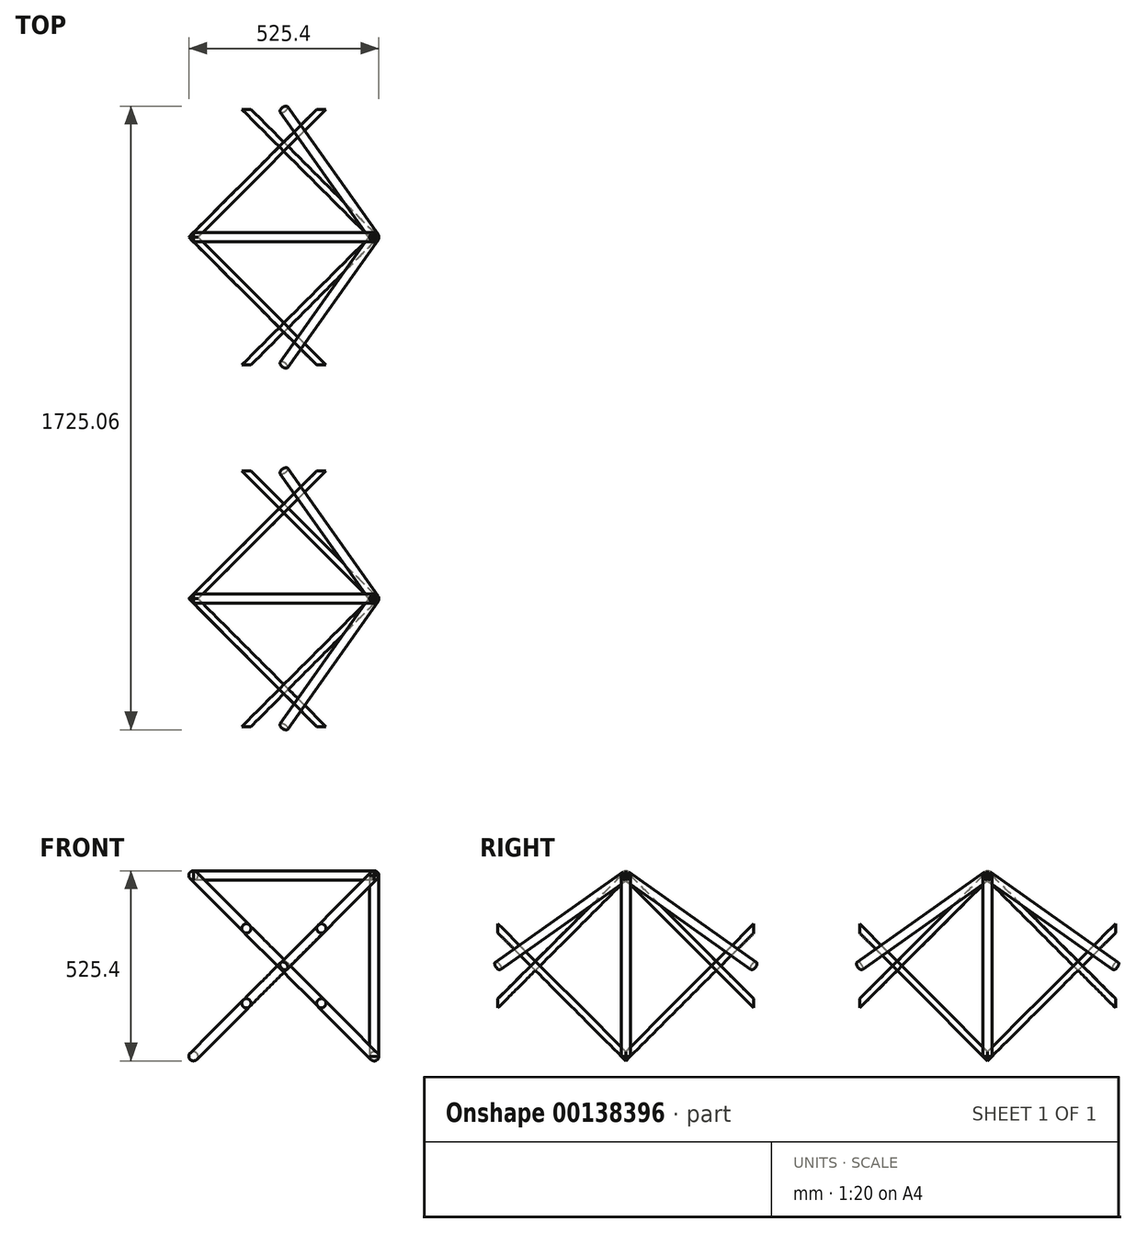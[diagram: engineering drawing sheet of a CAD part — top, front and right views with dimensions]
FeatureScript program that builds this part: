
annotation { "Feature Type Name" : "Feature", "Feature Type Description" : "" }
export const myFeature = defineFeature(function(context is Context, id is Id, definition is map)
    precondition{}
    {
        {
            var Q0;
            Q0=qCreatedBy(makeId("Front.planeOp"),FACE);
            var sketch = newSketch(context, id + "F0", { "sketchPlane" : qUnion([Q0])});
            skLineSegment(sketch, "E0.bottom", {"start": v(-250, 250) * mm, "end": v(250, 250) * mm});
            skLineSegment(sketch, "E0.top", {"start": v(-250, -250) * mm, "end": v(250, -250) * mm});
            skLineSegment(sketch, "E0.left", {"start": v(-250, 250) * mm, "end": v(-250, -250) * mm});
            skLineSegment(sketch, "E0.right", {"start": v(250, 250) * mm, "end": v(250, -250) * mm});
            skPoint(sketch, "E0.middle", {"position": v(0, 0) * mm});
            skSolve(sketch);
        }
        {
            var Q0;
            Q0=qCreatedBy(makeId("Right.planeOp"),FACE);
            var sketch = newSketch(context, id + "F1", { "sketchPlane" : qUnion([Q0])});
            skLineSegment(sketch, "E1", {"start": v(0, 0) * mm, "end": v(-500, 0) * mm});
            skSolve(sketch);
        }
        {
            var Q0;
            Q0=sQuery(id+"F0.wireOp",VERTEX,"E0.middle");
            var Q1;
            Q1=sQuery(id+"F1.wireOp",VERTEX,"E1.end");
            var Q2;
            Q2=sQuery(id+"F0.wireOp",VERTEX,"E0.right.start");
            cPlane(context, id + "F2", {"entities" : qUnion([Q0, Q1, Q2]), "cplaneType" : CPlaneType.THREE_POINT, "offset" : 25 * mm, "width" : 150 * mm, "height" : 150 * mm});
        }
        {
            var Q0;
            Q0=qCreatedBy(id+"F2.planeOp",FACE);
            var sketch = newSketch(context, id + "F3", { "sketchPlane" : qUnion([Q0])});
            skLineSegment(sketch, "E2.0", {"start": v(0, 0) * mm, "end": v(0, 500) * mm});
            skPoint(sketch, "E3.0", {"position": v(353.55, 0) * mm});
            skLineSegment(sketch, "E4", {"start": v(0, 500) * mm, "end": v(353.55, 0) * mm});
            skSolve(sketch);
        }
        {
            var Q0;
            Q0=makeQuery(id+"F0.imprint","IMPRINT",FACE,{"disambiguationData":[TD([[makeQuery(id+"F0.imprint","IMPRINT",EDGE,{"derivedFrom":sQuery(id+"F0.wireOp",EDGE,"E0.bottom")}),-1.0]])]});
            var sketch = newSketch(context, id + "F4", { "sketchPlane" : qUnion([Q0])});
            skPoint(sketch, "E5.0", {"position": v(250, 250) * mm});
            skCircle(sketch, "E6", {"center": v(250, 250) * mm, "radius": 12.7 * mm});
            skSolve(sketch);
        }
        {
            var Q0;
            Q0 = qSketchRegion(id + "F4", true);
            var Q1;
            Q1=sQuery(id+"F3.wireOp",EDGE,"E4");
            sweep(context, id + "F5", {"profiles" : qUnion([Q0]), "path" : qUnion([Q1])});
        }
        {
            var Q0;
            Q0=makeQuery(id+"F5.opSweep","SWEPT_BODY",BODY,{"disambiguationData":[OSD([sQuery(id+"F3.wireOp",EDGE,"E4"),sQuery(id+"F4.wireOp",EDGE,"E6")])]});
            var Q1;
            Q1=sQuery(id+"F1.wireOp",EDGE,"E1");
            circularPattern(context, id + "F6", {"entities" : qUnion([Q0]), "axis" : qUnion([Q1]), "angle" : 90 * degree, "instanceCount" : 4});
        }
        {
            var Q0;
            Q0=makeQuery(id+"F6.opPattern","COPY",BODY,{"derivedFrom":makeQuery(id+"F5.opSweep","SWEPT_BODY",BODY,{"disambiguationData":[OSD([sQuery(id+"F3.wireOp",EDGE,"E4"),sQuery(id+"F4.wireOp",EDGE,"E6")])]}),"instanceName":"1"});
            var Q1;
            Q1=makeQuery(id+"F6.opPattern","COPY",BODY,{"derivedFrom":makeQuery(id+"F5.opSweep","SWEPT_BODY",BODY,{"disambiguationData":[OSD([sQuery(id+"F3.wireOp",EDGE,"E4"),sQuery(id+"F4.wireOp",EDGE,"E6")])]}),"instanceName":"3"});
            var Q2;
            Q2=makeQuery(id+"F5.opSweep","SWEPT_BODY",BODY,{"disambiguationData":[OSD([sQuery(id+"F3.wireOp",EDGE,"E4"),sQuery(id+"F4.wireOp",EDGE,"E6")])]});
            var Q3;
            Q3=makeQuery(id+"F6.opPattern","COPY",BODY,{"derivedFrom":makeQuery(id+"F5.opSweep","SWEPT_BODY",BODY,{"disambiguationData":[OSD([sQuery(id+"F3.wireOp",EDGE,"E4"),sQuery(id+"F4.wireOp",EDGE,"E6")])]}),"instanceName":"2"});
            var Q4;
            Q4=makeQuery(id+"F0.imprint","IMPRINT",FACE,{"disambiguationData":[TD([[makeQuery(id+"F0.imprint","IMPRINT",EDGE,{"derivedFrom":sQuery(id+"F0.wireOp",EDGE,"E0.bottom")}),-1.0]])]});
            mirror(context, id + "F7", {"entities" : qUnion([Q0, Q1, Q2, Q3]), "mirrorPlane" : qUnion([Q4])});
        }
        {
            var Q0;
            Q0=qCreatedBy(makeId("Right.planeOp"),FACE);
            var sketch = newSketch(context, id + "F8", { "sketchPlane" : qUnion([Q0])});
            skPoint(sketch, "E7.0", {"position": v(0, 250) * mm});
            skCircle(sketch, "E8", {"center": v(0, 250) * mm, "radius": 12.7 * mm});
            skSolve(sketch);
        }
        {
            var Q0;
            Q0 = qSketchRegion(id + "F8", true);
            var Q1;
            Q1=makeQuery(id+"F5.opSweep","SWEPT_BODY",BODY,{"disambiguationData":[OSD([sQuery(id+"F3.wireOp",EDGE,"E4"),sQuery(id+"F4.wireOp",EDGE,"E6")])]});
            extrude(context, id + "F9", {"entities" : qUnion([Q0]), "endBound" : BoundingType.SYMMETRIC, "endBoundEntityBody" : qUnion([Q1]), "depth" : 500 * mm});
        }
        {
            var Q0;
            Q0=makeQuery(id+"F9.opExtrude","SWEPT_BODY",BODY,{"disambiguationData":[OSD([sQuery(id+"F8.wireOp",EDGE,"E8")])]});
            var Q1;
            Q1=sQuery(id+"F3.wireOp",EDGE,"E2.0");
            circularPattern(context, id + "F10", {"entities" : qUnion([Q0]), "axis" : qUnion([Q1]), "angle" : 90 * degree, "instanceCount" : 4});
        }
        {
            var Q0;
            Q0=qCreatedBy(makeId("Front.planeOp"),FACE);
            cPlane(context, id + "F11", {"entities" : qUnion([Q0]), "cplaneType" : CPlaneType.OFFSET, "offset" : 500 * mm, "width" : 150 * mm, "height" : 150 * mm});
        }
        {
            var Q0;
            Q0=makeQuery(id+"F7.opPattern","COPY",BODY,{"derivedFrom":makeQuery(id+"F6.opPattern","COPY",BODY,{"derivedFrom":makeQuery(id+"F5.opSweep","SWEPT_BODY",BODY,{"disambiguationData":[OSD([sQuery(id+"F3.wireOp",EDGE,"E4"),sQuery(id+"F4.wireOp",EDGE,"E6")])]}),"instanceName":"1"}),"instanceName":"1"});
            var Q1;
            Q1=makeQuery(id+"F6.opPattern","COPY",BODY,{"derivedFrom":makeQuery(id+"F5.opSweep","SWEPT_BODY",BODY,{"disambiguationData":[OSD([sQuery(id+"F3.wireOp",EDGE,"E4"),sQuery(id+"F4.wireOp",EDGE,"E6")])]}),"instanceName":"1"});
            var Q2;
            Q2=makeQuery(id+"F6.opPattern","COPY",BODY,{"derivedFrom":makeQuery(id+"F5.opSweep","SWEPT_BODY",BODY,{"disambiguationData":[OSD([sQuery(id+"F3.wireOp",EDGE,"E4"),sQuery(id+"F4.wireOp",EDGE,"E6")])]}),"instanceName":"3"});
            var Q3;
            Q3=makeQuery(id+"F10.opPattern","COPY",BODY,{"derivedFrom":makeQuery(id+"F9.opExtrude","SWEPT_BODY",BODY,{"disambiguationData":[OSD([sQuery(id+"F8.wireOp",EDGE,"E8")])]}),"instanceName":"3"});
            var Q4;
            Q4=makeQuery(id+"F5.opSweep","SWEPT_BODY",BODY,{"disambiguationData":[OSD([sQuery(id+"F3.wireOp",EDGE,"E4"),sQuery(id+"F4.wireOp",EDGE,"E6")])]});
            var Q5;
            Q5=makeQuery(id+"F7.opPattern","COPY",BODY,{"derivedFrom":makeQuery(id+"F5.opSweep","SWEPT_BODY",BODY,{"disambiguationData":[OSD([sQuery(id+"F3.wireOp",EDGE,"E4"),sQuery(id+"F4.wireOp",EDGE,"E6")])]}),"instanceName":"1"});
            var Q6;
            Q6=makeQuery(id+"F6.opPattern","COPY",BODY,{"derivedFrom":makeQuery(id+"F5.opSweep","SWEPT_BODY",BODY,{"disambiguationData":[OSD([sQuery(id+"F3.wireOp",EDGE,"E4"),sQuery(id+"F4.wireOp",EDGE,"E6")])]}),"instanceName":"2"});
            var Q7;
            Q7=makeQuery(id+"F7.opPattern","COPY",BODY,{"derivedFrom":makeQuery(id+"F6.opPattern","COPY",BODY,{"derivedFrom":makeQuery(id+"F5.opSweep","SWEPT_BODY",BODY,{"disambiguationData":[OSD([sQuery(id+"F3.wireOp",EDGE,"E4"),sQuery(id+"F4.wireOp",EDGE,"E6")])]}),"instanceName":"2"}),"instanceName":"1"});
            var Q8;
            Q8=makeQuery(id+"F7.opPattern","COPY",BODY,{"derivedFrom":makeQuery(id+"F6.opPattern","COPY",BODY,{"derivedFrom":makeQuery(id+"F5.opSweep","SWEPT_BODY",BODY,{"disambiguationData":[OSD([sQuery(id+"F3.wireOp",EDGE,"E4"),sQuery(id+"F4.wireOp",EDGE,"E6")])]}),"instanceName":"3"}),"instanceName":"1"});
            var Q9;
            Q9=makeQuery(id+"F9.opExtrude","SWEPT_BODY",BODY,{"disambiguationData":[OSD([sQuery(id+"F8.wireOp",EDGE,"E8")])]});
            var Q10;
            Q10=makeQuery(id+"F10.opPattern","COPY",BODY,{"derivedFrom":makeQuery(id+"F9.opExtrude","SWEPT_BODY",BODY,{"disambiguationData":[OSD([sQuery(id+"F8.wireOp",EDGE,"E8")])]}),"instanceName":"1"});
            var Q11;
            Q11=makeQuery(id+"F10.opPattern","COPY",BODY,{"derivedFrom":makeQuery(id+"F9.opExtrude","SWEPT_BODY",BODY,{"disambiguationData":[OSD([sQuery(id+"F8.wireOp",EDGE,"E8")])]}),"instanceName":"2"});
            var Q12;
            Q12=qCreatedBy(id+"F11.planeOp",FACE);
            mirror(context, id + "F12", {"entities" : qUnion([Q0, Q1, Q2, Q3, Q4, Q5, Q6, Q7, Q8, Q9, Q10, Q11]), "mirrorPlane" : qUnion([Q12])});
        }
    });
